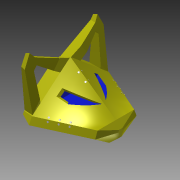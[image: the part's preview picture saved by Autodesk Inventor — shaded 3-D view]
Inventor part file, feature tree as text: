
AUTODESK INVENTOR PART (.ipt)
format: ipt  version: 2016 (Build 200138000, 138)  size: 745,472 bytes
history: native  units: in
note: dims shown in document units (in); Inventor stores cm internally (conversion verified against a paired STEP export)
features: sketch x22, extrude x16, plane x9, projected_geometry x5, loft x4, other x3, chamfer x1, mirror x1, emboss x1, fillet x1
ambient origin geometry x8: Origin, YZ Plane, XZ Plane, XY Plane, X Axis, Y Axis, Z Axis, Center Point
bodies: Solid1 (feature_tree)
feature tree (63):
  sketch  "Sketch1"  dims[d0=0.7559in d1=0.7559in]
  plane  "Work Plane1"
  loft  "Loft1"
  extrude  "Extrusion1"  Depth=0.2in
  plane  "Work Plane4"
  loft  "Loft2"
  plane  "Work Plane5"
  loft  "Loft3"
  loft  "Loft4"
  extrude  "Extrusion2"  TaperAngle=0.0deg  [1 undecoded]
  plane  "Work Plane6"
  extrude  "Extrusion3"  Depth=1.0in
  extrude  "Extrusion4"  Depth=1.0651in
  extrude  "Extrusion5"  Depth=0.962in
  plane  "Work Plane7"
  extrude  "Extrusion6"  Depth=0.075in
  plane  "Work Plane8"
  other  "Work Axis1"
  plane  "Work Plane9"
  chamfer  "Chamfer1"  Distance=0.45in
  extrude  "Extrusion7"  Depth=0.01in
  mirror  "Mirror3"
  extrude  "Extrusion8"  Depth=0.01in
  plane  "Work Plane10"
  extrude  "Extrusion9"  TaperAngle=0.0deg  [1 undecoded]
  plane  "Work Plane11"
  extrude  "Extrusion10"  Depth=0.07in
  extrude  "Extrusion11"  TaperAngle=0.0deg  [1 undecoded]
  extrude  "Extrusion12"  Depth=0.01in
  extrude  "Extrusion13"  TaperAngle=150.0deg  [1 undecoded]
  emboss  "Emboss1"
  extrude  "Extrusion16"  TaperAngle=150.0deg  [1 undecoded]
  extrude  "Extrusion17"  Depth=0.7in
  extrude  "Extrusion18"  Depth=0.05in
  fillet  "Fillet2"  Radius=0.05in
  sketch  "Sketch2"  dims[d2=0.9963in d3=0.2in]
  sketch  "Sketch3"  dims[d4=0.5in d6=0.08in]
  sketch  "Sketch4"  dims[d7=0.55in d8=150.0deg]
  other  "Edges1"
  sketch  "Sketch5"  dims[d9=150.0deg d14=0.33in]
  projected_geometry  "Projected Loop1"
  other  "Edges2"
  sketch  "Sketch6"  dims[d15=0.66in d18=0.0in d19=90.0deg]
  sketch  "Sketch7"  dims[d20=0.0in d21=90.0deg d22=1.0in]
  sketch  "Sketch8"  dims[d26=1.0651in d28=1.0651in]
  sketch  "Sketch9"  dims[d29=0.0in d30=0.962in]
  sketch  "Sketch10"  dims[d31=0.962in d32=0.075in]
  sketch  "Sketch11"  dims[d33=0.15in]
  sketch  "Sketch12"  dims[d34=0.06in]
  sketch  "Sketch13"  dims[d35=0.1in]
  projected_geometry  "Projected Loop2"
  projected_geometry  "Projected Loop3"
  sketch  "Sketch14"  dims[d36=0.05in d37=0.45in d38=0.0in]
  projected_geometry  "Projected Loop4"
  sketch  "Sketch15"  dims[d39=0.0625in d40=0.01in]
  sketch  "Sketch16"  dims[d41=0.075in d42=0.01in]
  sketch  "Sketch17"  dims[d43=0.0in d44=90.0deg d45=0.0in d46=90.0deg]
  sketch  "Sketch18"  dims[d47=0.2in d48=0.07in]
  sketch  "Sketch19"  dims[d49=0.0in d50=90.0deg d51=0.0in d52=90.0deg]
  sketch  "Sketch23"  dims[d53=0.01in d54=0.01in]
  projected_geometry  "Projected Loop6"
  sketch  "Sketch24"  dims[d55=0.0344in d56=150.0deg]
  sketch  "Sketch25"  dims[d57=60.0deg d58=150.0deg d59=0.7in d60=0.05in d61=0.05in d62=0.05in d63=0.05in d64=0.05in d65=0.01in d66=0.0in d67=90.0deg d68=0.0in d69=90.0deg d70=0.1in d71=0.4in d72=0.15in d73=0.05in d74=0.0in d75=0.02in d77=0.15in d78=0.02in d79=0.1in d80=0.1in d81=0.1in d82=0.02in d83=0.15in d84=0.05in d85=0.0in d86=0.045in d87=0.0in d88=0.025in d89=0.0in d90=0.02in d91=0.02in d92=0.005in d93=0.0in d94=90.0deg d95=0.4466in d96=1.0in d97=0.0in d98=1.0in d99=0.0in d100=0.6528in d101=0.0in d102=0.0in d103=1.0in d104=0.0in d106=90.0deg d107=1.0in d108=0.0in d109=1.65in d110=0.1in d111=0.1in d112=0.0in d113=0.1in d114=0.075in d115=0.0in d116=0.05in d117=0.0in d123=0.84in d124=0.8in d125=0.0in d126=0.0in d127=1.0in d128=0.0in d130=0.225in d131=-0.0206in d133=0.2125in d134=0.1125in d135=0.07in d136=0.1in d137=0.02in d138=0.125in d139=45.0deg]
note: 5 required parameter values undecoded (feature->parameter linkage not recoverable at this tier; creation-order binding heuristic only, values carry confidence <= 0.55)
